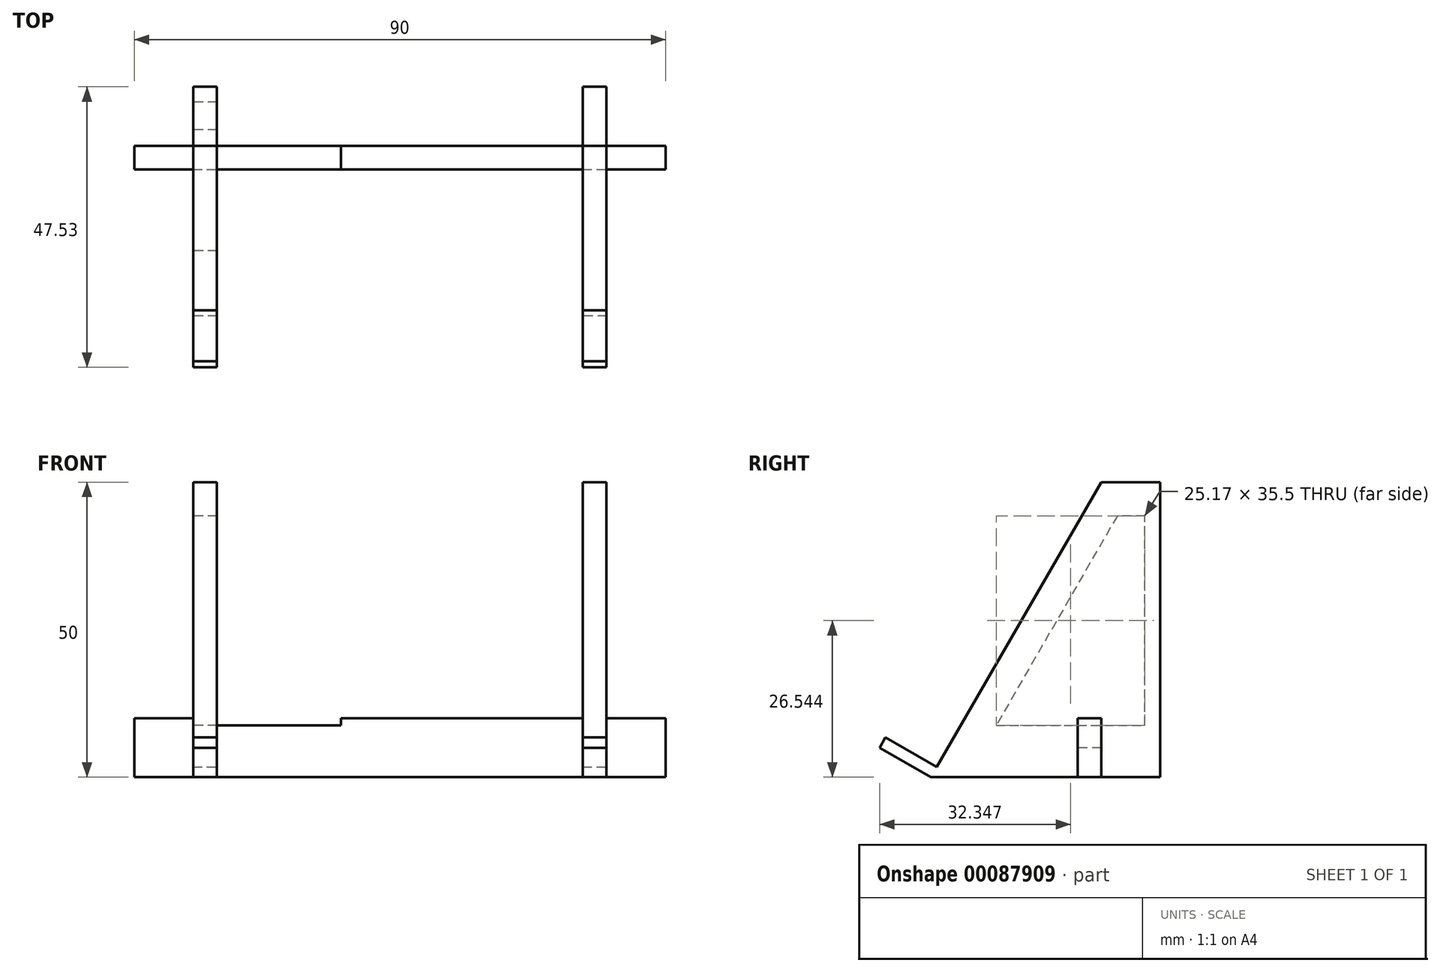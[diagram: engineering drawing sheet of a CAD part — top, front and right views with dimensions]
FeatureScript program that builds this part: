
annotation { "Feature Type Name" : "Feature", "Feature Type Description" : "" }
export const myFeature = defineFeature(function(context is Context, id is Id, definition is map)
    precondition{}
    {
        {
            var Q0;
            Q0=qCreatedBy(makeId("Top.planeOp"),FACE);
            var sketch = newSketch(context, id + "F0", { "sketchPlane" : qUnion([Q0])});
            skLineSegment(sketch, "E0.bottom", {"start": v(0, 0) * mm, "end": v(90, 0) * mm});
            skLineSegment(sketch, "E0.top", {"start": v(0, -4) * mm, "end": v(90, -4) * mm});
            skLineSegment(sketch, "E0.left", {"start": v(0, 0) * mm, "end": v(0, -4) * mm});
            skLineSegment(sketch, "E0.right", {"start": v(90, 0) * mm, "end": v(90, -4) * mm});
            skLineSegment(sketch, "E1.bottom", {"start": v(10, 10) * mm, "end": v(14, 10) * mm});
            skLineSegment(sketch, "E1.top", {"start": v(10, -50) * mm, "end": v(14, -50) * mm});
            skLineSegment(sketch, "E1.left", {"start": v(10, 10) * mm, "end": v(10, -50) * mm});
            skLineSegment(sketch, "E1.right", {"start": v(14, 10) * mm, "end": v(14, -50) * mm});
            skLineSegment(sketch, "E2.bottom", {"start": v(76, 10) * mm, "end": v(80, 10) * mm});
            skLineSegment(sketch, "E2.top", {"start": v(76, -50) * mm, "end": v(80, -50) * mm});
            skLineSegment(sketch, "E2.left", {"start": v(76, 10) * mm, "end": v(76, -50) * mm});
            skLineSegment(sketch, "E2.right", {"start": v(80, 10) * mm, "end": v(80, -50) * mm});
            skSolve(sketch);
        }
        {
            var Q0;
            {var subQ0=sQuery(id+"F0.wireOp",EDGE,"E0.left");Q0=makeQuery(id+"F0.imprint","IMPRINT",FACE,{"disambiguationData":[TD([[makeQuery(id+"F0.imprint","IMPRINT",EDGE,{"derivedFrom":subQ0}),1.0]])]});}
            var Q1;
            {var subQ0=sQuery(id+"F0.wireOp",EDGE,"E1.right");var subQ1=sQuery(id+"F0.wireOp",EDGE,"E0.bottom");var subQ2=makeQuery(id+"F0.imprint","INTERSECT",VERTEX,{"derivedFrom":[subQ1,subQ0]});Q1=makeQuery(id+"F0.imprint","IMPRINT",FACE,{"disambiguationData":[TD([[makeQuery(id+"F0.imprint","IMPRINT",EDGE,{"disambiguationData":[TD([[subQ2,-1.0]])],"derivedFrom":subQ1}),-1.0]])]});}
            var Q2;
            {var subQ0=sQuery(id+"F0.wireOp",EDGE,"E0.right");Q2=makeQuery(id+"F0.imprint","IMPRINT",FACE,{"disambiguationData":[TD([[makeQuery(id+"F0.imprint","IMPRINT",EDGE,{"derivedFrom":subQ0}),-1.0]])]});}
            extrude(context, id + "F1", {"entities" : qUnion([Q0, Q1, Q2]), "depth" : 10 * mm});
        }
        {
            var Q0;
            {var subQ5=sQuery(id+"F0.wireOp",EDGE,"E1.bottom");Q0=makeQuery(id+"F0.imprint","IMPRINT",FACE,{"disambiguationData":[TD([[makeQuery(id+"F0.imprint","IMPRINT",EDGE,{"derivedFrom":subQ5}),-1.0]])]});}
            var Q1;
            {var subQ0=sQuery(id+"F0.wireOp",EDGE,"E1.left");var subQ1=sQuery(id+"F0.wireOp",EDGE,"E0.bottom");var subQ2=makeQuery(id+"F0.imprint","INTERSECT",VERTEX,{"derivedFrom":[subQ1,subQ0]});Q1=makeQuery(id+"F0.imprint","IMPRINT",FACE,{"disambiguationData":[TD([[makeQuery(id+"F0.imprint","IMPRINT",EDGE,{"disambiguationData":[TD([[subQ2,-1.0]])],"derivedFrom":subQ1}),-1.0]])]});}
            var Q2;
            {var subQ5=sQuery(id+"F0.wireOp",EDGE,"E1.top");Q2=makeQuery(id+"F0.imprint","IMPRINT",FACE,{"disambiguationData":[TD([[makeQuery(id+"F0.imprint","IMPRINT",EDGE,{"derivedFrom":subQ5}),1.0]])]});}
            var Q3;
            {var subQ5=sQuery(id+"F0.wireOp",EDGE,"E2.bottom");Q3=makeQuery(id+"F0.imprint","IMPRINT",FACE,{"disambiguationData":[TD([[makeQuery(id+"F0.imprint","IMPRINT",EDGE,{"derivedFrom":subQ5}),-1.0]])]});}
            var Q4;
            {var subQ0=sQuery(id+"F0.wireOp",EDGE,"E2.left");var subQ1=sQuery(id+"F0.wireOp",EDGE,"E0.bottom");var subQ2=makeQuery(id+"F0.imprint","INTERSECT",VERTEX,{"derivedFrom":[subQ1,subQ0]});Q4=makeQuery(id+"F0.imprint","IMPRINT",FACE,{"disambiguationData":[TD([[makeQuery(id+"F0.imprint","IMPRINT",EDGE,{"disambiguationData":[TD([[subQ2,-1.0]])],"derivedFrom":subQ1}),-1.0]])]});}
            var Q5;
            {var subQ5=sQuery(id+"F0.wireOp",EDGE,"E2.top");Q5=makeQuery(id+"F0.imprint","IMPRINT",FACE,{"disambiguationData":[TD([[makeQuery(id+"F0.imprint","IMPRINT",EDGE,{"derivedFrom":subQ5}),1.0]])]});}
            extrude(context, id + "F2", {"entities" : qUnion([Q0, Q1, Q2, Q3, Q4, Q5]), "depth" : 50 * mm});
        }
        {
            var Q0;
            Q0=makeQuery(id+"F2.opExtrude","CAP_EDGE",EDGE,{"disambiguationData":[OSD([sQuery(id+"F0.wireOp",EDGE,"E1.top")])],"isStart":false});
            var Q1;
            Q1=makeQuery(id+"F2.opExtrude","CAP_EDGE",EDGE,{"disambiguationData":[OSD([sQuery(id+"F0.wireOp",EDGE,"E2.top")])],"isStart":false});
            chamfer(context, id + "F3", {"entities" : qUnion([Q0, Q1]), "chamferType" : ChamferType.OFFSET_ANGLE, "width" : 50 * mm, "oppositeDirection" : false, "angle" : 60 * degree});
        }
        {
            var Q0;
            Q0=makeQuery(id+"F3.opChamfer","BLEND_FACE",FACE,{"disambiguationData":[OSD([sQuery(id+"F0.wireOp",EDGE,"E1.top")])]});
            var sketch = newSketch(context, id + "F4", { "sketchPlane" : qUnion([Q0])});
            skLineSegment(sketch, "E3.bottom", {"start": v(10, -14.43) * mm, "end": v(14, -14.43) * mm});
            skLineSegment(sketch, "E3.top", {"start": v(10, -12.43) * mm, "end": v(14, -12.43) * mm});
            skLineSegment(sketch, "E3.left", {"start": v(10, -14.43) * mm, "end": v(10, -12.43) * mm});
            skLineSegment(sketch, "E3.right", {"start": v(14, -14.43) * mm, "end": v(14, -12.43) * mm});
            skSolve(sketch);
        }
        {
            var Q0;
            Q0=makeQuery(id+"F4.imprint","IMPRINT",FACE,{"disambiguationData":[TD([[makeQuery(id+"F4.imprint","IMPRINT",EDGE,{"derivedFrom":sQuery(id+"F4.wireOp",EDGE,"E3.bottom")}),-1.0]])]});
            extrude(context, id + "F5", {"entities" : qUnion([Q0]), "operationType" : NewBodyOperationType.ADD, "depth" : 10 * mm});
        }
        {
            var Q0;
            Q0=makeQuery(id+"F3.opChamfer","BLEND_FACE",FACE,{"disambiguationData":[OSD([sQuery(id+"F0.wireOp",EDGE,"E2.top")])]});
            var sketch = newSketch(context, id + "F6", { "sketchPlane" : qUnion([Q0])});
            skLineSegment(sketch, "E4.bottom", {"start": v(76, -14.43) * mm, "end": v(80, -14.43) * mm});
            skLineSegment(sketch, "E4.top", {"start": v(76, -12.43) * mm, "end": v(80, -12.43) * mm});
            skLineSegment(sketch, "E4.left", {"start": v(76, -14.43) * mm, "end": v(76, -12.43) * mm});
            skLineSegment(sketch, "E4.right", {"start": v(80, -14.43) * mm, "end": v(80, -12.43) * mm});
            skSolve(sketch);
        }
        {
            var Q0;
            Q0=makeQuery(id+"F6.imprint","IMPRINT",FACE,{"disambiguationData":[TD([[makeQuery(id+"F6.imprint","IMPRINT",EDGE,{"derivedFrom":sQuery(id+"F6.wireOp",EDGE,"E4.bottom")}),-1.0]])]});
            extrude(context, id + "F7", {"entities" : qUnion([Q0]), "operationType" : NewBodyOperationType.ADD, "depth" : 10 * mm});
        }
        {
            var Q0;
            {var subQ0=sQuery(id+"F0.wireOp",EDGE,"E1.left");var subQ1=sQuery(id+"F0.wireOp",EDGE,"E0.bottom");var subQ2=makeQuery(id+"F0.imprint","INTERSECT",VERTEX,{"derivedFrom":[subQ1,subQ0]});Q0=makeQuery(id+"F0.imprint","IMPRINT",FACE,{"disambiguationData":[TD([[makeQuery(id+"F0.imprint","IMPRINT",EDGE,{"disambiguationData":[TD([[subQ2,-1.0]])],"derivedFrom":subQ1}),-1.0]])]});}
            var Q1;
            {var subQ0=sQuery(id+"F0.wireOp",EDGE,"E2.left");var subQ1=sQuery(id+"F0.wireOp",EDGE,"E0.bottom");var subQ2=makeQuery(id+"F0.imprint","INTERSECT",VERTEX,{"derivedFrom":[subQ1,subQ0]});Q1=makeQuery(id+"F0.imprint","IMPRINT",FACE,{"disambiguationData":[TD([[makeQuery(id+"F0.imprint","IMPRINT",EDGE,{"disambiguationData":[TD([[subQ2,-1.0]])],"derivedFrom":subQ1}),-1.0]])]});}
            extrude(context, id + "F8", {"entities" : qUnion([Q0, Q1]), "depth" : 5 * mm});
        }
        {
            var Q0;
            {var subQ0=sQuery(id+"F0.wireOp",EDGE,"E1.left");var subQ1=sQuery(id+"F0.wireOp",EDGE,"E0.bottom");var subQ2=makeQuery(id+"F0.imprint","INTERSECT",VERTEX,{"derivedFrom":[subQ1,subQ0]});Q0=makeQuery(id+"F0.imprint","IMPRINT",FACE,{"disambiguationData":[TD([[makeQuery(id+"F0.imprint","IMPRINT",EDGE,{"disambiguationData":[TD([[subQ2,-1.0]])],"derivedFrom":subQ1}),-1.0]])]});}
            extrude(context, id + "F9", {"entities" : qUnion([Q0]), "operationType" : NewBodyOperationType.REMOVE, "depth" : 5 * mm});
        }
        {
            var Q0;
            Q0=makeQuery(id+"F5.boolean.opBoolean","MERGE",FACE,{"derivedFrom":[makeQuery(id+"F2.opExtrude","SWEPT_FACE",FACE,{"disambiguationData":[OSD([sQuery(id+"F0.wireOp",EDGE,"E1.left")])]}),makeQuery(id+"F5.opExtrude","SWEPT_FACE",FACE,{"disambiguationData":[OSD([sQuery(id+"F4.wireOp",EDGE,"E3.left")])]})]});
            var sketch = newSketch(context, id + "F10", { "sketchPlane" : qUnion([Q0])});
            skLineSegment(sketch, "E5", {"start": v(-7.4, 8.8) * mm, "end": v(17.77, 8.8) * mm});
            skLineSegment(sketch, "E6", {"start": v(17.77, 8.8) * mm, "end": v(-2.73, 44.3) * mm});
            skLineSegment(sketch, "E7", {"start": v(-2.73, 44.3) * mm, "end": v(-7.4, 44.3) * mm});
            skLineSegment(sketch, "E8", {"start": v(-7.4, 44.3) * mm, "end": v(-7.4, 8.8) * mm});
            skSolve(sketch);
        }
        {
            var Q0;
            Q0=makeQuery(id+"F10.imprint","IMPRINT",FACE,{"disambiguationData":[TD([[makeQuery(id+"F10.imprint","IMPRINT",EDGE,{"derivedFrom":sQuery(id+"F10.wireOp",EDGE,"E5")}),1.0]])]});
            extrude(context, id + "F11", {"entities" : qUnion([Q0]), "operationType" : NewBodyOperationType.REMOVE, "oppositeDirection" : true, "depth" : 25 * mm});
        }
    });
